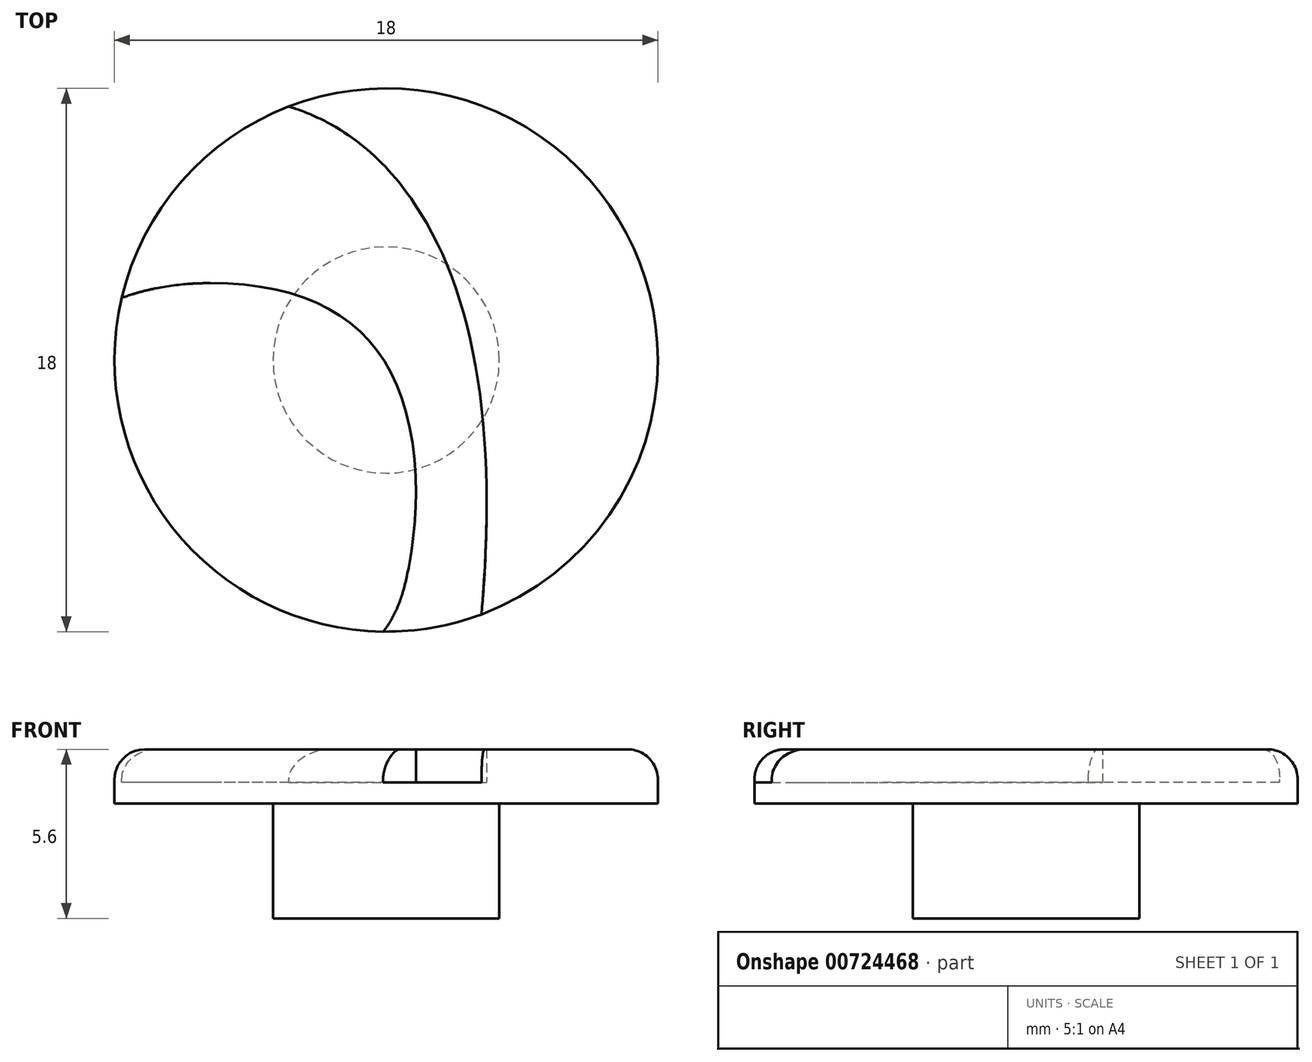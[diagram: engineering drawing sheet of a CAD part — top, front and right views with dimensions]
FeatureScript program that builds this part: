
annotation { "Feature Type Name" : "Feature", "Feature Type Description" : "" }
export const myFeature = defineFeature(function(context is Context, id is Id, definition is map)
    precondition{}
    {
        {
            var Q0;
            Q0=qCreatedBy(makeId("Top.planeOp"),FACE);
            var sketch = newSketch(context, id + "F0", { "sketchPlane" : qUnion([Q0])});
            skCircle(sketch, "E0", {"center": v(0, 0) * mm, "radius": 9 * mm});
            skSolve(sketch);
        }
        {
            var Q0;
            Q0 = qSketchRegion(id + "F0", true);
            extrude(context, id + "F1", {"entities" : qUnion([Q0]), "oppositeDirection" : true, "depth" : 1.8 * mm, "offsetDistance" : 25 * mm});
        }
        {
            var Q0;
            Q0=makeQuery(id+"F1.opExtrude","CAP_FACE",FACE,{"disambiguationData":[OSD([sQuery(id+"F0.wireOp",EDGE,"E0")])],"isStart":false});
            var sketch = newSketch(context, id + "F2", { "sketchPlane" : qUnion([Q0])});
            skCircle(sketch, "E1", {"center": v(0, 0) * mm, "radius": 3.75 * mm});
            skSolve(sketch);
        }
        {
            var Q0;
            Q0 = qSketchRegion(id + "F2", true);
            extrude(context, id + "F3", {"entities" : qUnion([Q0]), "operationType" : NewBodyOperationType.ADD, "depth" : 3.8 * mm, "offsetDistance" : 25 * mm});
        }
        {
            var Q0;
            Q0=makeQuery(id+"F1.opExtrude","CAP_FACE",FACE,{"disambiguationData":[OSD([sQuery(id+"F0.wireOp",EDGE,"E0")])],"isStart":true});
            var sketch = newSketch(context, id + "F4", { "sketchPlane" : qUnion([Q0])});
            skText(sketch, "E2", { "text": "ימת", "fontName": "Tinos-Bold.ttf"});
            skLineSegment(sketch, "E3", {"start": v(-45.79, 4) * mm, "end": v(51.23, 4) * mm, "construction": true});
            skLineSegment(sketch, "E4.MirrorCS", {"start": v(-45.79, -4) * mm, "end": v(51.23, -4) * mm, "construction": true});
            const initialGuessF4  = {"E2": [-0.03136, -0.01554, 1, 0, 0.03109]};
            skSetInitialGuess(sketch, initialGuessF4);
            skSolve(sketch);
        }
        {
            var Q0;
            Q0 = qSketchRegion(id + "F4", true);
            extrude(context, id + "F5", {"entities" : qUnion([Q0]), "operationType" : NewBodyOperationType.REMOVE, "oppositeDirection" : true, "depth" : 1.1 * mm, "offsetDistance" : 25 * mm});
        }
        {
            var Q0;
            Q0=makeQuery(id+"F1.opExtrude","CAP_EDGE",EDGE,{"disambiguationData":[OSD([sQuery(id+"F0.wireOp",EDGE,"E0")])],"isStart":true});
            fillet(context, id + "F6", {"entities" : qUnion([Q0]), "radius" : 1 * mm, "tangentPropagation" : true, "allowEdgeOverflow" : false});
        }
    });
